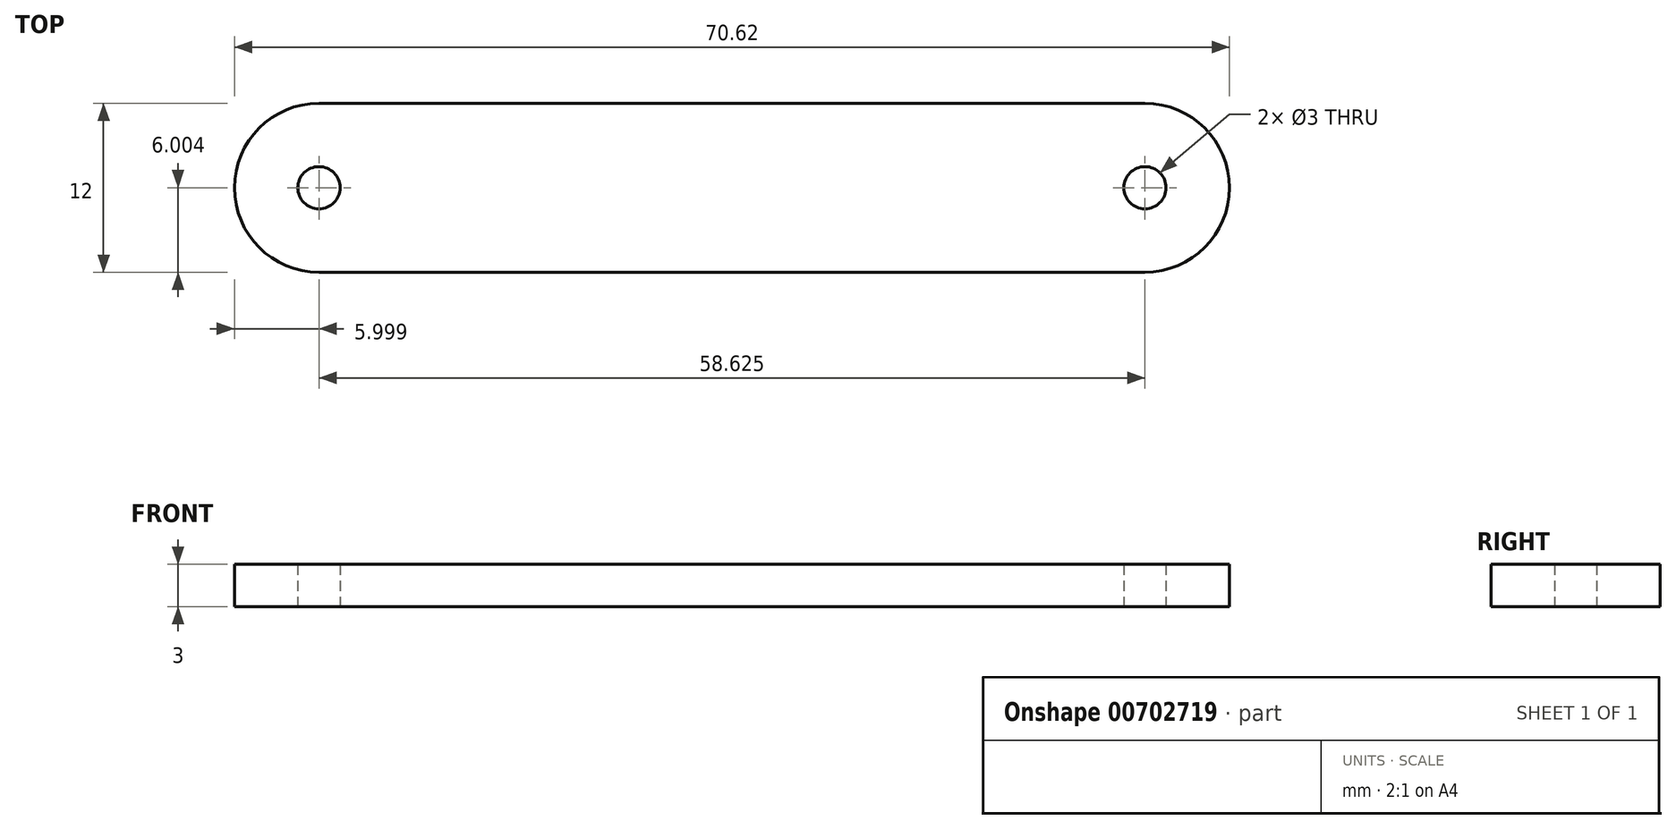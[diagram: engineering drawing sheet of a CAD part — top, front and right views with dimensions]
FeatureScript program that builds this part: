
annotation { "Feature Type Name" : "Feature", "Feature Type Description" : "" }
export const myFeature = defineFeature(function(context is Context, id is Id, definition is map)
    precondition{}
    {
        {
            var Q0;
            Q0=qCreatedBy(makeId("Top.planeOp"),FACE);
            var sketch = newSketch(context, id + "F0", { "sketchPlane" : qUnion([Q0])});
            skArc(sketch, "E0", {"start": v(-22.84, 16.02) * mm, "mid": v(-28.84, 10.02) * mm, "end": v(-22.84, 4.02) * mm});
            skArc(sketch, "E1", {"start": v(35.78, 4.02) * mm, "mid": v(41.78, 10.02) * mm, "end": v(35.78, 16.02) * mm});
            skCircle(sketch, "E2", {"center": v(35.78, 10.02) * mm, "radius": 1.5 * mm});
            skCircle(sketch, "E3", {"center": v(-22.84, 10.02) * mm, "radius": 1.5 * mm});
            skLineSegment(sketch, "E4", {"start": v(-22.84, 16.02) * mm, "end": v(35.78, 16.02) * mm});
            skLineSegment(sketch, "E5", {"start": v(35.78, 4.02) * mm, "end": v(-22.84, 4.02) * mm});
            skSolve(sketch);
        }
        {
            var Q0;
            Q0=makeQuery(id+"F0.imprint","IMPRINT",FACE,{"disambiguationData":[TD([[makeQuery(id+"F0.imprint","IMPRINT",EDGE,{"derivedFrom":sQuery(id+"F0.wireOp",EDGE,"E0")}),1.0]])]});
            extrude(context, id + "F1", {"entities" : qUnion([Q0]), "depth" : 3 * mm, "offsetDistance" : 25.4 * mm});
        }
    });
